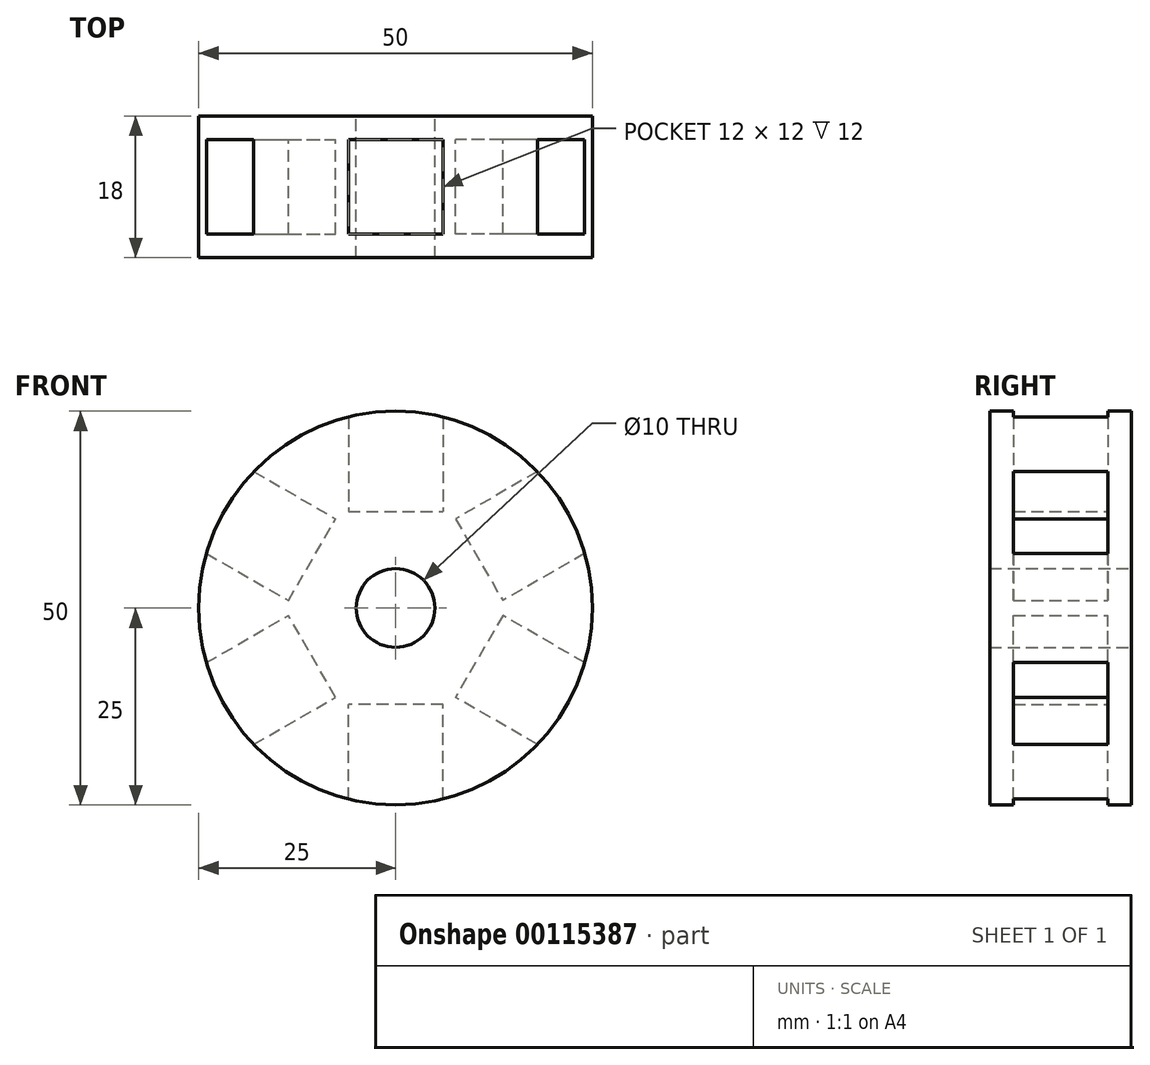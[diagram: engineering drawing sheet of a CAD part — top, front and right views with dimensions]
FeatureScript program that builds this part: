
annotation { "Feature Type Name" : "Feature", "Feature Type Description" : "" }
export const myFeature = defineFeature(function(context is Context, id is Id, definition is map)
    precondition{}
    {
        {
            var Q0;
            Q0=qCreatedBy(makeId("Front.planeOp"),FACE);
            var sketch = newSketch(context, id + "F0", { "sketchPlane" : qUnion([Q0])});
            skCircle(sketch, "E0", {"center": v(0, 0) * mm, "radius": 25 * mm});
            skLineSegment(sketch, "E1.bottom", {"start": v(-6, 24.27) * mm, "end": v(6, 24.27) * mm});
            skLineSegment(sketch, "E1.top", {"start": v(-6, 12.27) * mm, "end": v(6, 12.27) * mm});
            skLineSegment(sketch, "E1.left", {"start": v(-6, 24.27) * mm, "end": v(-6, 12.27) * mm});
            skLineSegment(sketch, "E1.right", {"start": v(6, 24.27) * mm, "end": v(6, 12.27) * mm});
            skLineSegment(sketch, "E2.1.0", {"start": v(-24.02, 6.94) * mm, "end": v(-18.02, 17.33) * mm});
            skLineSegment(sketch, "E2.1.1", {"start": v(-24.02, 6.94) * mm, "end": v(-13.63, 0.94) * mm});
            skLineSegment(sketch, "E2.1.2", {"start": v(-18.02, 17.33) * mm, "end": v(-7.63, 11.33) * mm});
            skLineSegment(sketch, "E2.1.3", {"start": v(-13.63, 0.94) * mm, "end": v(-7.63, 11.33) * mm});
            skLineSegment(sketch, "E2.2.0", {"start": v(-18.02, -17.33) * mm, "end": v(-24.02, -6.94) * mm});
            skLineSegment(sketch, "E2.2.1", {"start": v(-18.02, -17.33) * mm, "end": v(-7.63, -11.33) * mm});
            skLineSegment(sketch, "E2.2.2", {"start": v(-24.02, -6.94) * mm, "end": v(-13.63, -0.94) * mm});
            skLineSegment(sketch, "E2.2.3", {"start": v(-7.63, -11.33) * mm, "end": v(-13.63, -0.94) * mm});
            skLineSegment(sketch, "E2.3.0", {"start": v(6, -24.27) * mm, "end": v(-6, -24.27) * mm});
            skLineSegment(sketch, "E2.3.1", {"start": v(6, -24.27) * mm, "end": v(6, -12.27) * mm});
            skLineSegment(sketch, "E2.3.2", {"start": v(-6, -24.27) * mm, "end": v(-6, -12.27) * mm});
            skLineSegment(sketch, "E2.3.3", {"start": v(6, -12.27) * mm, "end": v(-6, -12.27) * mm});
            skLineSegment(sketch, "E2.4.0", {"start": v(24.02, -6.94) * mm, "end": v(18.02, -17.33) * mm});
            skLineSegment(sketch, "E2.4.1", {"start": v(24.02, -6.94) * mm, "end": v(13.63, -0.94) * mm});
            skLineSegment(sketch, "E2.4.2", {"start": v(18.02, -17.33) * mm, "end": v(7.63, -11.33) * mm});
            skLineSegment(sketch, "E2.4.3", {"start": v(13.63, -0.94) * mm, "end": v(7.63, -11.33) * mm});
            skLineSegment(sketch, "E2.5.0", {"start": v(18.02, 17.33) * mm, "end": v(24.02, 6.94) * mm});
            skLineSegment(sketch, "E2.5.1", {"start": v(18.02, 17.33) * mm, "end": v(7.63, 11.33) * mm});
            skLineSegment(sketch, "E2.5.2", {"start": v(24.02, 6.94) * mm, "end": v(13.63, 0.94) * mm});
            skLineSegment(sketch, "E2.5.3", {"start": v(7.63, 11.33) * mm, "end": v(13.63, 0.94) * mm});
            skCircle(sketch, "E3", {"center": v(0, 0) * mm, "radius": 5 * mm});
            skSolve(sketch);
        }
        {
            var Q0;
            Q0=makeQuery(id+"F0.imprint","IMPRINT",FACE,{"disambiguationData":[TD([[makeQuery(id+"F0.imprint","IMPRINT",EDGE,{"derivedFrom":sQuery(id+"F0.wireOp",EDGE,"E1.top")}),-1.0]])]});
            extrude(context, id + "F1", {"entities" : qUnion([Q0]), "endBound" : BoundingType.SYMMETRIC, "depth" : 12 * mm});
        }
        {
            var Q0;
            Q0=makeQuery(id+"F1.opExtrude","CAP_FACE",FACE,{"disambiguationData":[OSD([sQuery(id+"F0.wireOp",EDGE,"E0"),sQuery(id+"F0.wireOp",EDGE,"E1.top"),sQuery(id+"F0.wireOp",EDGE,"E1.left"),sQuery(id+"F0.wireOp",EDGE,"E1.right"),sQuery(id+"F0.wireOp",EDGE,"E2.1.1"),sQuery(id+"F0.wireOp",EDGE,"E2.1.2"),sQuery(id+"F0.wireOp",EDGE,"E2.1.3"),sQuery(id+"F0.wireOp",EDGE,"E2.2.1"),sQuery(id+"F0.wireOp",EDGE,"E2.2.2"),sQuery(id+"F0.wireOp",EDGE,"E2.2.3"),sQuery(id+"F0.wireOp",EDGE,"E2.3.1"),sQuery(id+"F0.wireOp",EDGE,"E2.3.2"),sQuery(id+"F0.wireOp",EDGE,"E2.3.3"),sQuery(id+"F0.wireOp",EDGE,"E2.4.1"),sQuery(id+"F0.wireOp",EDGE,"E2.4.2"),sQuery(id+"F0.wireOp",EDGE,"E2.4.3"),sQuery(id+"F0.wireOp",EDGE,"E2.5.1"),sQuery(id+"F0.wireOp",EDGE,"E2.5.2"),sQuery(id+"F0.wireOp",EDGE,"E2.5.3"),sQuery(id+"F0.wireOp",EDGE,"E3")])],"isStart":false});
            var sketch = newSketch(context, id + "F2", { "sketchPlane" : qUnion([Q0])});
            skCircle(sketch, "E4", {"center": v(0, 0) * mm, "radius": 25 * mm});
            skSolve(sketch);
        }
        {
            var Q0;
            Q0 = qSketchRegion(id + "F2", true);
            extrude(context, id + "F3", {"entities" : qUnion([Q0]), "operationType" : NewBodyOperationType.ADD, "depth" : 3 * mm});
        }
        {
            var Q0;
            Q0=makeQuery(id+"F1.opExtrude","CAP_FACE",FACE,{"disambiguationData":[OSD([sQuery(id+"F0.wireOp",EDGE,"E0"),sQuery(id+"F0.wireOp",EDGE,"E1.top"),sQuery(id+"F0.wireOp",EDGE,"E1.left"),sQuery(id+"F0.wireOp",EDGE,"E1.right"),sQuery(id+"F0.wireOp",EDGE,"E2.1.1"),sQuery(id+"F0.wireOp",EDGE,"E2.1.2"),sQuery(id+"F0.wireOp",EDGE,"E2.1.3"),sQuery(id+"F0.wireOp",EDGE,"E2.2.1"),sQuery(id+"F0.wireOp",EDGE,"E2.2.2"),sQuery(id+"F0.wireOp",EDGE,"E2.2.3"),sQuery(id+"F0.wireOp",EDGE,"E2.3.1"),sQuery(id+"F0.wireOp",EDGE,"E2.3.2"),sQuery(id+"F0.wireOp",EDGE,"E2.3.3"),sQuery(id+"F0.wireOp",EDGE,"E2.4.1"),sQuery(id+"F0.wireOp",EDGE,"E2.4.2"),sQuery(id+"F0.wireOp",EDGE,"E2.4.3"),sQuery(id+"F0.wireOp",EDGE,"E2.5.1"),sQuery(id+"F0.wireOp",EDGE,"E2.5.2"),sQuery(id+"F0.wireOp",EDGE,"E2.5.3"),sQuery(id+"F0.wireOp",EDGE,"E3")])],"isStart":true});
            var sketch = newSketch(context, id + "F4", { "sketchPlane" : qUnion([Q0])});
            skCircle(sketch, "E5", {"center": v(0, 0) * mm, "radius": 25 * mm});
            skSolve(sketch);
        }
        {
            var Q0;
            Q0 = qSketchRegion(id + "F4", true);
            extrude(context, id + "F5", {"entities" : qUnion([Q0]), "operationType" : NewBodyOperationType.ADD, "depth" : 3 * mm});
        }
        {
            var Q0;
            Q0=makeQuery(id+"F0.imprint","IMPRINT",FACE,{"disambiguationData":[TD([[makeQuery(id+"F0.imprint","IMPRINT",EDGE,{"derivedFrom":sQuery(id+"F0.wireOp",EDGE,"E3")}),1.0]])]});
            extrude(context, id + "F6", {"entities" : qUnion([Q0]), "operationType" : NewBodyOperationType.REMOVE, "endBound" : BoundingType.SYMMETRIC, "depth" : 18 * mm});
        }
    });
